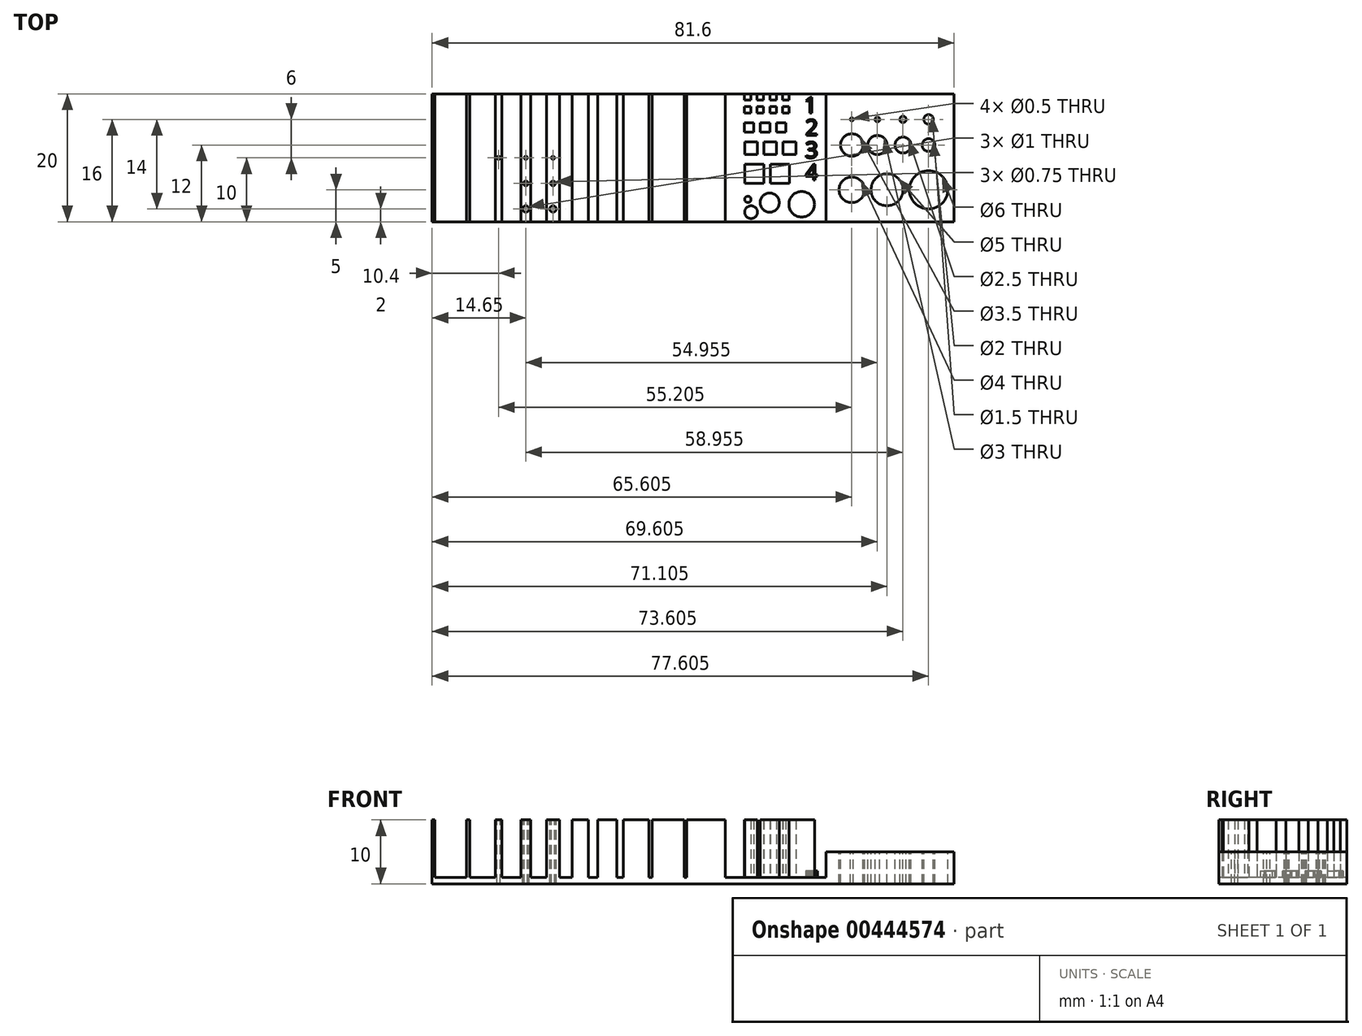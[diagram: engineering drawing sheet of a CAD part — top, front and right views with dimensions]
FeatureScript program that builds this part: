
annotation { "Feature Type Name" : "Feature", "Feature Type Description" : "" }
export const myFeature = defineFeature(function(context is Context, id is Id, definition is map)
    precondition{}
    {
        {
            var Q0;
            Q0=qCreatedBy(makeId("Top.planeOp"),FACE);
            var sketch = newSketch(context, id + "F0", { "sketchPlane" : qUnion([Q0])});
            skLineSegment(sketch, "E0.bottom", {"start": v(0, 0) * mm, "end": v(81.6, 0) * mm});
            skLineSegment(sketch, "E0.top", {"start": v(0, 20) * mm, "end": v(81.6, 20) * mm});
            skLineSegment(sketch, "E0.left", {"start": v(0, 0) * mm, "end": v(0, 20) * mm});
            skLineSegment(sketch, "E0.right", {"start": v(81.6, 0) * mm, "end": v(81.6, 20) * mm});
            skSolve(sketch);
        }
        {
            var Q0;
            Q0=makeQuery(id+"F0.imprint","IMPRINT",FACE,{"disambiguationData":[TD([[makeQuery(id+"F0.imprint","IMPRINT",EDGE,{"derivedFrom":sQuery(id+"F0.wireOp",EDGE,"E0.bottom")}),1.0]])]});
            extrude(context, id + "F1", {"entities" : qUnion([Q0]), "depth" : 1 * mm});
        }
        {
            var Q0;
            Q0=makeQuery(id+"F1.opExtrude","CAP_FACE",FACE,{"disambiguationData":[OSD([sQuery(id+"F0.wireOp",EDGE,"E0.bottom"),sQuery(id+"F0.wireOp",EDGE,"E0.top"),sQuery(id+"F0.wireOp",EDGE,"E0.left"),sQuery(id+"F0.wireOp",EDGE,"E0.right")])],"isStart":false});
            var sketch = newSketch(context, id + "F2", { "sketchPlane" : qUnion([Q0])});
            skLineSegment(sketch, "E1.bottom", {"start": v(0, 20) * mm, "end": v(0.4, 20) * mm});
            skLineSegment(sketch, "E1.top", {"start": v(0, 0) * mm, "end": v(0.4, 0) * mm});
            skLineSegment(sketch, "E1.left", {"start": v(0, 20) * mm, "end": v(0, 0) * mm});
            skLineSegment(sketch, "E1.right", {"start": v(0.4, 20) * mm, "end": v(0.4, 0) * mm});
            skLineSegment(sketch, "E2.bottom", {"start": v(5.4, 20) * mm, "end": v(5.9, 20) * mm});
            skLineSegment(sketch, "E2.top", {"start": v(5.4, 0) * mm, "end": v(5.9, 0) * mm});
            skLineSegment(sketch, "E2.left", {"start": v(5.4, 20) * mm, "end": v(5.4, 0) * mm});
            skLineSegment(sketch, "E2.right", {"start": v(5.9, 20) * mm, "end": v(5.9, 0) * mm});
            skLineSegment(sketch, "E3.bottom", {"start": v(9.9, 20) * mm, "end": v(10.9, 20) * mm});
            skLineSegment(sketch, "E3.top", {"start": v(9.9, 0) * mm, "end": v(10.9, 0) * mm});
            skLineSegment(sketch, "E3.left", {"start": v(9.9, 20) * mm, "end": v(9.9, 0) * mm});
            skLineSegment(sketch, "E3.right", {"start": v(10.9, 20) * mm, "end": v(10.9, 0) * mm});
            skLineSegment(sketch, "E4.bottom", {"start": v(13.9, 20) * mm, "end": v(15.4, 20) * mm});
            skLineSegment(sketch, "E4.top", {"start": v(13.9, 0) * mm, "end": v(15.4, 0) * mm});
            skLineSegment(sketch, "E4.left", {"start": v(13.9, 20) * mm, "end": v(13.9, 0) * mm});
            skLineSegment(sketch, "E4.right", {"start": v(15.4, 20) * mm, "end": v(15.4, 0) * mm});
            skLineSegment(sketch, "E5.bottom", {"start": v(17.9, 20) * mm, "end": v(19.9, 20) * mm});
            skLineSegment(sketch, "E5.top", {"start": v(17.9, 0) * mm, "end": v(19.9, 0) * mm});
            skLineSegment(sketch, "E5.left", {"start": v(17.9, 20) * mm, "end": v(17.9, 0) * mm});
            skLineSegment(sketch, "E5.right", {"start": v(19.9, 20) * mm, "end": v(19.9, 0) * mm});
            skLineSegment(sketch, "E6.bottom", {"start": v(21.9, 20) * mm, "end": v(24.4, 20) * mm});
            skLineSegment(sketch, "E6.top", {"start": v(21.9, 0) * mm, "end": v(24.4, 0) * mm});
            skLineSegment(sketch, "E6.left", {"start": v(21.9, 20) * mm, "end": v(21.9, 0) * mm});
            skLineSegment(sketch, "E6.right", {"start": v(24.4, 20) * mm, "end": v(24.4, 0) * mm});
            skLineSegment(sketch, "E7.bottom", {"start": v(25.9, 20) * mm, "end": v(28.9, 20) * mm});
            skLineSegment(sketch, "E7.top", {"start": v(25.9, 0) * mm, "end": v(28.9, 0) * mm});
            skLineSegment(sketch, "E7.left", {"start": v(25.9, 20) * mm, "end": v(25.9, 0) * mm});
            skLineSegment(sketch, "E7.right", {"start": v(28.9, 20) * mm, "end": v(28.9, 0) * mm});
            skLineSegment(sketch, "E8.bottom", {"start": v(29.9, 20) * mm, "end": v(33.9, 20) * mm});
            skLineSegment(sketch, "E8.top", {"start": v(29.9, 0) * mm, "end": v(33.9, 0) * mm});
            skLineSegment(sketch, "E8.left", {"start": v(29.9, 20) * mm, "end": v(29.9, 0) * mm});
            skLineSegment(sketch, "E8.right", {"start": v(33.9, 20) * mm, "end": v(33.9, 0) * mm});
            skLineSegment(sketch, "E9.bottom", {"start": v(34.4, 20) * mm, "end": v(39.4, 20) * mm});
            skLineSegment(sketch, "E9.top", {"start": v(34.4, 0) * mm, "end": v(39.4, 0) * mm});
            skLineSegment(sketch, "E9.left", {"start": v(34.4, 20) * mm, "end": v(34.4, 0) * mm});
            skLineSegment(sketch, "E9.right", {"start": v(39.4, 20) * mm, "end": v(39.4, 0) * mm});
            skLineSegment(sketch, "E10.bottom", {"start": v(39.8, 20) * mm, "end": v(45.8, 20) * mm});
            skLineSegment(sketch, "E10.top", {"start": v(39.8, 0) * mm, "end": v(45.8, 0) * mm});
            skLineSegment(sketch, "E10.left", {"start": v(39.8, 20) * mm, "end": v(39.8, 0) * mm});
            skLineSegment(sketch, "E10.right", {"start": v(45.8, 20) * mm, "end": v(45.8, 0) * mm});
            skLineSegment(sketch, "E11.bottom", {"start": v(48.8, 20) * mm, "end": v(49.8, 20) * mm});
            skLineSegment(sketch, "E11.top", {"start": v(48.8, 19) * mm, "end": v(49.8, 19) * mm});
            skLineSegment(sketch, "E11.left", {"start": v(48.8, 20) * mm, "end": v(48.8, 19) * mm});
            skLineSegment(sketch, "E11.right", {"start": v(49.8, 20) * mm, "end": v(49.8, 19) * mm});
            skLineSegment(sketch, "E12.bottom", {"start": v(50.8, 20) * mm, "end": v(51.8, 20) * mm});
            skLineSegment(sketch, "E12.top", {"start": v(50.8, 19) * mm, "end": v(51.8, 19) * mm});
            skLineSegment(sketch, "E12.left", {"start": v(50.8, 20) * mm, "end": v(50.8, 19) * mm});
            skLineSegment(sketch, "E12.right", {"start": v(51.8, 20) * mm, "end": v(51.8, 19) * mm});
            skLineSegment(sketch, "E13.bottom", {"start": v(52.8, 20) * mm, "end": v(53.8, 20) * mm});
            skLineSegment(sketch, "E13.top", {"start": v(52.8, 19) * mm, "end": v(53.8, 19) * mm});
            skLineSegment(sketch, "E13.left", {"start": v(52.8, 20) * mm, "end": v(52.8, 19) * mm});
            skLineSegment(sketch, "E13.right", {"start": v(53.8, 20) * mm, "end": v(53.8, 19) * mm});
            skLineSegment(sketch, "E14.bottom", {"start": v(54.8, 20) * mm, "end": v(55.8, 20) * mm});
            skLineSegment(sketch, "E14.top", {"start": v(54.8, 19) * mm, "end": v(55.8, 19) * mm});
            skLineSegment(sketch, "E14.left", {"start": v(54.8, 20) * mm, "end": v(54.8, 19) * mm});
            skLineSegment(sketch, "E14.right", {"start": v(55.8, 20) * mm, "end": v(55.8, 19) * mm});
            skLineSegment(sketch, "E15.bottom", {"start": v(48.8, 18) * mm, "end": v(49.8, 18) * mm});
            skLineSegment(sketch, "E15.top", {"start": v(48.8, 17) * mm, "end": v(49.8, 17) * mm});
            skLineSegment(sketch, "E15.left", {"start": v(48.8, 18) * mm, "end": v(48.8, 17) * mm});
            skLineSegment(sketch, "E15.right", {"start": v(49.8, 18) * mm, "end": v(49.8, 17) * mm});
            skLineSegment(sketch, "E16.bottom", {"start": v(50.8, 18) * mm, "end": v(51.8, 18) * mm});
            skLineSegment(sketch, "E16.top", {"start": v(50.8, 17) * mm, "end": v(51.8, 17) * mm});
            skLineSegment(sketch, "E16.left", {"start": v(50.8, 18) * mm, "end": v(50.8, 17) * mm});
            skLineSegment(sketch, "E16.right", {"start": v(51.8, 18) * mm, "end": v(51.8, 17) * mm});
            skLineSegment(sketch, "E17.bottom", {"start": v(52.8, 18) * mm, "end": v(53.8, 18) * mm});
            skLineSegment(sketch, "E17.top", {"start": v(52.8, 17) * mm, "end": v(53.8, 17) * mm});
            skLineSegment(sketch, "E17.left", {"start": v(52.8, 18) * mm, "end": v(52.8, 17) * mm});
            skLineSegment(sketch, "E17.right", {"start": v(53.8, 18) * mm, "end": v(53.8, 17) * mm});
            skLineSegment(sketch, "E18.bottom", {"start": v(54.8, 18) * mm, "end": v(55.8, 18) * mm});
            skLineSegment(sketch, "E18.top", {"start": v(54.8, 17) * mm, "end": v(55.8, 17) * mm});
            skLineSegment(sketch, "E18.left", {"start": v(54.8, 18) * mm, "end": v(54.8, 17) * mm});
            skLineSegment(sketch, "E18.right", {"start": v(55.8, 18) * mm, "end": v(55.8, 17) * mm});
            skLineSegment(sketch, "E19.bottom", {"start": v(48.8, 15.5) * mm, "end": v(50.3, 15.5) * mm});
            skLineSegment(sketch, "E19.top", {"start": v(48.8, 14) * mm, "end": v(50.3, 14) * mm});
            skLineSegment(sketch, "E19.left", {"start": v(48.8, 15.5) * mm, "end": v(48.8, 14) * mm});
            skLineSegment(sketch, "E19.right", {"start": v(50.3, 15.5) * mm, "end": v(50.3, 14) * mm});
            skLineSegment(sketch, "E20.bottom", {"start": v(51.3, 15.5) * mm, "end": v(52.8, 15.5) * mm});
            skLineSegment(sketch, "E20.top", {"start": v(51.3, 14) * mm, "end": v(52.8, 14) * mm});
            skLineSegment(sketch, "E20.left", {"start": v(51.3, 15.5) * mm, "end": v(51.3, 14) * mm});
            skLineSegment(sketch, "E20.right", {"start": v(52.8, 15.5) * mm, "end": v(52.8, 14) * mm});
            skLineSegment(sketch, "E21.bottom", {"start": v(53.8, 15.5) * mm, "end": v(55.3, 15.5) * mm});
            skLineSegment(sketch, "E21.top", {"start": v(53.8, 14) * mm, "end": v(55.3, 14) * mm});
            skLineSegment(sketch, "E21.left", {"start": v(53.8, 15.5) * mm, "end": v(53.8, 14) * mm});
            skLineSegment(sketch, "E21.right", {"start": v(55.3, 15.5) * mm, "end": v(55.3, 14) * mm});
            skLineSegment(sketch, "E22.bottom", {"start": v(48.86, 12.5) * mm, "end": v(50.86, 12.5) * mm});
            skLineSegment(sketch, "E22.top", {"start": v(48.86, 10.5) * mm, "end": v(50.86, 10.5) * mm});
            skLineSegment(sketch, "E22.left", {"start": v(48.86, 12.5) * mm, "end": v(48.86, 10.5) * mm});
            skLineSegment(sketch, "E22.right", {"start": v(50.86, 12.5) * mm, "end": v(50.86, 10.5) * mm});
            skLineSegment(sketch, "E23.bottom", {"start": v(51.86, 12.5) * mm, "end": v(53.86, 12.5) * mm});
            skLineSegment(sketch, "E23.top", {"start": v(51.86, 10.5) * mm, "end": v(53.86, 10.5) * mm});
            skLineSegment(sketch, "E23.left", {"start": v(51.86, 12.5) * mm, "end": v(51.86, 10.5) * mm});
            skLineSegment(sketch, "E23.right", {"start": v(53.86, 12.5) * mm, "end": v(53.86, 10.5) * mm});
            skLineSegment(sketch, "E24.bottom", {"start": v(54.86, 12.5) * mm, "end": v(56.86, 12.5) * mm});
            skLineSegment(sketch, "E24.top", {"start": v(54.86, 10.5) * mm, "end": v(56.86, 10.5) * mm});
            skLineSegment(sketch, "E24.left", {"start": v(54.86, 12.5) * mm, "end": v(54.86, 10.5) * mm});
            skLineSegment(sketch, "E24.right", {"start": v(56.86, 12.5) * mm, "end": v(56.86, 10.5) * mm});
            skLineSegment(sketch, "E25.bottom", {"start": v(48.86, 9) * mm, "end": v(51.86, 9) * mm});
            skLineSegment(sketch, "E25.top", {"start": v(48.86, 6) * mm, "end": v(51.86, 6) * mm});
            skLineSegment(sketch, "E25.left", {"start": v(48.86, 9) * mm, "end": v(48.86, 6) * mm});
            skLineSegment(sketch, "E25.right", {"start": v(51.86, 9) * mm, "end": v(51.86, 6) * mm});
            skLineSegment(sketch, "E26.bottom", {"start": v(52.86, 9) * mm, "end": v(55.86, 9) * mm});
            skLineSegment(sketch, "E26.top", {"start": v(52.86, 6) * mm, "end": v(55.86, 6) * mm});
            skLineSegment(sketch, "E26.left", {"start": v(52.86, 9) * mm, "end": v(52.86, 6) * mm});
            skLineSegment(sketch, "E26.right", {"start": v(55.86, 9) * mm, "end": v(55.86, 6) * mm});
            skCircle(sketch, "E27", {"center": v(49.36, 3.5) * mm, "radius": 0.5 * mm});
            skCircle(sketch, "E28", {"center": v(49.86, 1.5) * mm, "radius": 1 * mm});
            skCircle(sketch, "E29", {"center": v(52.77, 3) * mm, "radius": 1.5 * mm});
            skCircle(sketch, "E30", {"center": v(57.77, 2.74) * mm, "radius": 2 * mm});
            skSolve(sketch);
        }
        {
            var Q0;
            Q0=makeQuery(id+"F2.imprint","IMPRINT",FACE,{"disambiguationData":[TD([[makeQuery(id+"F2.imprint","IMPRINT",EDGE,{"derivedFrom":sQuery(id+"F2.wireOp",EDGE,"E1.bottom")}),-1.0]])]});
            var Q1;
            Q1=makeQuery(id+"F2.imprint","IMPRINT",FACE,{"disambiguationData":[TD([[makeQuery(id+"F2.imprint","IMPRINT",EDGE,{"derivedFrom":sQuery(id+"F2.wireOp",EDGE,"E2.bottom")}),-1.0]])]});
            var Q2;
            Q2=makeQuery(id+"F2.imprint","IMPRINT",FACE,{"disambiguationData":[TD([[makeQuery(id+"F2.imprint","IMPRINT",EDGE,{"derivedFrom":sQuery(id+"F2.wireOp",EDGE,"E3.bottom")}),-1.0]])]});
            var Q3;
            Q3=makeQuery(id+"F2.imprint","IMPRINT",FACE,{"disambiguationData":[TD([[makeQuery(id+"F2.imprint","IMPRINT",EDGE,{"derivedFrom":sQuery(id+"F2.wireOp",EDGE,"E4.bottom")}),-1.0]])]});
            var Q4;
            Q4=makeQuery(id+"F2.imprint","IMPRINT",FACE,{"disambiguationData":[TD([[makeQuery(id+"F2.imprint","IMPRINT",EDGE,{"derivedFrom":sQuery(id+"F2.wireOp",EDGE,"E5.bottom")}),-1.0]])]});
            var Q5;
            Q5=makeQuery(id+"F2.imprint","IMPRINT",FACE,{"disambiguationData":[TD([[makeQuery(id+"F2.imprint","IMPRINT",EDGE,{"derivedFrom":sQuery(id+"F2.wireOp",EDGE,"E6.bottom")}),-1.0]])]});
            var Q6;
            Q6=makeQuery(id+"F2.imprint","IMPRINT",FACE,{"disambiguationData":[TD([[makeQuery(id+"F2.imprint","IMPRINT",EDGE,{"derivedFrom":sQuery(id+"F2.wireOp",EDGE,"E7.bottom")}),-1.0]])]});
            var Q7;
            Q7=makeQuery(id+"F2.imprint","IMPRINT",FACE,{"disambiguationData":[TD([[makeQuery(id+"F2.imprint","IMPRINT",EDGE,{"derivedFrom":sQuery(id+"F2.wireOp",EDGE,"E8.bottom")}),-1.0]])]});
            var Q8;
            Q8=makeQuery(id+"F2.imprint","IMPRINT",FACE,{"disambiguationData":[TD([[makeQuery(id+"F2.imprint","IMPRINT",EDGE,{"derivedFrom":sQuery(id+"F2.wireOp",EDGE,"E9.bottom")}),-1.0]])]});
            var Q9;
            Q9=makeQuery(id+"F2.imprint","IMPRINT",FACE,{"disambiguationData":[TD([[makeQuery(id+"F2.imprint","IMPRINT",EDGE,{"derivedFrom":sQuery(id+"F2.wireOp",EDGE,"E10.bottom")}),-1.0]])]});
            var Q10;
            Q10=makeQuery(id+"F2.imprint","IMPRINT",FACE,{"disambiguationData":[TD([[makeQuery(id+"F2.imprint","IMPRINT",EDGE,{"derivedFrom":sQuery(id+"F2.wireOp",EDGE,"E15.bottom")}),-1.0]])]});
            var Q11;
            Q11=makeQuery(id+"F2.imprint","IMPRINT",FACE,{"disambiguationData":[TD([[makeQuery(id+"F2.imprint","IMPRINT",EDGE,{"derivedFrom":sQuery(id+"F2.wireOp",EDGE,"E11.bottom")}),-1.0]])]});
            var Q12;
            Q12=makeQuery(id+"F2.imprint","IMPRINT",FACE,{"disambiguationData":[TD([[makeQuery(id+"F2.imprint","IMPRINT",EDGE,{"derivedFrom":sQuery(id+"F2.wireOp",EDGE,"E12.bottom")}),-1.0]])]});
            var Q13;
            Q13=makeQuery(id+"F2.imprint","IMPRINT",FACE,{"disambiguationData":[TD([[makeQuery(id+"F2.imprint","IMPRINT",EDGE,{"derivedFrom":sQuery(id+"F2.wireOp",EDGE,"E13.bottom")}),-1.0]])]});
            var Q14;
            Q14=makeQuery(id+"F2.imprint","IMPRINT",FACE,{"disambiguationData":[TD([[makeQuery(id+"F2.imprint","IMPRINT",EDGE,{"derivedFrom":sQuery(id+"F2.wireOp",EDGE,"E14.bottom")}),-1.0]])]});
            var Q15;
            Q15=makeQuery(id+"F2.imprint","IMPRINT",FACE,{"disambiguationData":[TD([[makeQuery(id+"F2.imprint","IMPRINT",EDGE,{"derivedFrom":sQuery(id+"F2.wireOp",EDGE,"E18.bottom")}),-1.0]])]});
            var Q16;
            Q16=makeQuery(id+"F2.imprint","IMPRINT",FACE,{"disambiguationData":[TD([[makeQuery(id+"F2.imprint","IMPRINT",EDGE,{"derivedFrom":sQuery(id+"F2.wireOp",EDGE,"E17.bottom")}),-1.0]])]});
            var Q17;
            Q17=makeQuery(id+"F2.imprint","IMPRINT",FACE,{"disambiguationData":[TD([[makeQuery(id+"F2.imprint","IMPRINT",EDGE,{"derivedFrom":sQuery(id+"F2.wireOp",EDGE,"E16.bottom")}),-1.0]])]});
            var Q18;
            Q18=makeQuery(id+"F2.imprint","IMPRINT",FACE,{"disambiguationData":[TD([[makeQuery(id+"F2.imprint","IMPRINT",EDGE,{"derivedFrom":sQuery(id+"F2.wireOp",EDGE,"E19.bottom")}),-1.0]])]});
            var Q19;
            Q19=makeQuery(id+"F2.imprint","IMPRINT",FACE,{"disambiguationData":[TD([[makeQuery(id+"F2.imprint","IMPRINT",EDGE,{"derivedFrom":sQuery(id+"F2.wireOp",EDGE,"E20.bottom")}),-1.0]])]});
            var Q20;
            Q20=makeQuery(id+"F2.imprint","IMPRINT",FACE,{"disambiguationData":[TD([[makeQuery(id+"F2.imprint","IMPRINT",EDGE,{"derivedFrom":sQuery(id+"F2.wireOp",EDGE,"E21.bottom")}),-1.0]])]});
            var Q21;
            Q21=makeQuery(id+"F2.imprint","IMPRINT",FACE,{"disambiguationData":[TD([[makeQuery(id+"F2.imprint","IMPRINT",EDGE,{"derivedFrom":sQuery(id+"F2.wireOp",EDGE,"E22.bottom")}),-1.0]])]});
            var Q22;
            Q22=makeQuery(id+"F2.imprint","IMPRINT",FACE,{"disambiguationData":[TD([[makeQuery(id+"F2.imprint","IMPRINT",EDGE,{"derivedFrom":sQuery(id+"F2.wireOp",EDGE,"E23.bottom")}),-1.0]])]});
            var Q23;
            Q23=makeQuery(id+"F2.imprint","IMPRINT",FACE,{"disambiguationData":[TD([[makeQuery(id+"F2.imprint","IMPRINT",EDGE,{"derivedFrom":sQuery(id+"F2.wireOp",EDGE,"E24.bottom")}),-1.0]])]});
            var Q24;
            Q24=makeQuery(id+"F2.imprint","IMPRINT",FACE,{"disambiguationData":[TD([[makeQuery(id+"F2.imprint","IMPRINT",EDGE,{"derivedFrom":sQuery(id+"F2.wireOp",EDGE,"E25.bottom")}),-1.0]])]});
            var Q25;
            Q25=makeQuery(id+"F2.imprint","IMPRINT",FACE,{"disambiguationData":[TD([[makeQuery(id+"F2.imprint","IMPRINT",EDGE,{"derivedFrom":sQuery(id+"F2.wireOp",EDGE,"E26.bottom")}),-1.0]])]});
            var Q26;
            Q26=makeQuery(id+"F2.imprint","IMPRINT",FACE,{"disambiguationData":[TD([[makeQuery(id+"F2.imprint","IMPRINT",EDGE,{"derivedFrom":sQuery(id+"F2.wireOp",EDGE,"E27")}),1.0]])]});
            var Q27;
            Q27=makeQuery(id+"F2.imprint","IMPRINT",FACE,{"disambiguationData":[TD([[makeQuery(id+"F2.imprint","IMPRINT",EDGE,{"derivedFrom":sQuery(id+"F2.wireOp",EDGE,"E28")}),1.0]])]});
            var Q28;
            Q28=makeQuery(id+"F2.imprint","IMPRINT",FACE,{"disambiguationData":[TD([[makeQuery(id+"F2.imprint","IMPRINT",EDGE,{"derivedFrom":sQuery(id+"F2.wireOp",EDGE,"E29")}),1.0]])]});
            var Q29;
            Q29=makeQuery(id+"F2.imprint","IMPRINT",FACE,{"disambiguationData":[TD([[makeQuery(id+"F2.imprint","IMPRINT",EDGE,{"derivedFrom":sQuery(id+"F2.wireOp",EDGE,"E30")}),1.0]])]});
            extrude(context, id + "F3", {"entities" : qUnion([Q0, Q1, Q2, Q3, Q4, Q5, Q6, Q7, Q8, Q9, Q10, Q11, Q12, Q13, Q14, Q15, Q16, Q17, Q18, Q19, Q20, Q21, Q22, Q23, Q24, Q25, Q26, Q27, Q28, Q29]), "operationType" : NewBodyOperationType.ADD, "depth" : 9 * mm});
        }
        {
            var Q0;
            {var subQ0=sQuery(id+"F0.wireOp",EDGE,"E0.right");var subQ1=sQuery(id+"F0.wireOp",EDGE,"E0.top");var subQ2=sQuery(id+"F0.wireOp",EDGE,"E0.bottom");Q0=makeQuery(id+"F3.boolean.opBoolean","SPLIT",FACE,{"disambiguationData":[TD([makeQuery(id+"F1.opExtrude","SWEPT_FACE",FACE,{"disambiguationData":[OSD([subQ0])]})])],"derivedFrom":makeQuery(id+"F1.opExtrude","CAP_FACE",FACE,{"disambiguationData":[OSD([subQ2,subQ1,sQuery(id+"F0.wireOp",EDGE,"E0.left"),subQ0])],"isStart":false})});}
            var sketch = newSketch(context, id + "F4", { "sketchPlane" : qUnion([Q0])});
            skLineSegment(sketch, "E31.bottom", {"start": v(81.6, 20) * mm, "end": v(61.6, 20) * mm});
            skLineSegment(sketch, "E31.top", {"start": v(81.6, 0) * mm, "end": v(61.6, 0) * mm});
            skLineSegment(sketch, "E31.left", {"start": v(81.6, 20) * mm, "end": v(81.6, 0) * mm});
            skLineSegment(sketch, "E31.right", {"start": v(61.6, 20) * mm, "end": v(61.6, 0) * mm});
            skSolve(sketch);
        }
        {
            var Q0;
            Q0=makeQuery(id+"F4.imprint","IMPRINT",FACE,{"disambiguationData":[TD([[makeQuery(id+"F4.imprint","IMPRINT",EDGE,{"derivedFrom":sQuery(id+"F4.wireOp",EDGE,"E31.bottom")}),-1.0]])]});
            extrude(context, id + "F5", {"entities" : qUnion([Q0]), "operationType" : NewBodyOperationType.ADD, "depth" : 4 * mm});
        }
        {
            var Q0;
            Q0=makeQuery(id+"F3.opExtrude","CAP_FACE",FACE,{"disambiguationData":[OSD([sQuery(id+"F2.wireOp",EDGE,"E3.bottom"),sQuery(id+"F2.wireOp",EDGE,"E3.top"),sQuery(id+"F2.wireOp",EDGE,"E3.left"),sQuery(id+"F2.wireOp",EDGE,"E3.right")])],"isStart":false});
            var sketch = newSketch(context, id + "F6", { "sketchPlane" : qUnion([Q0])});
            skCircle(sketch, "E32", {"center": v(10.4, 10) * mm, "radius": 0.25 * mm});
            skSolve(sketch);
        }
        {
            var Q0;
            Q0=makeQuery(id+"F6.imprint","IMPRINT",FACE,{"disambiguationData":[TD([[makeQuery(id+"F6.imprint","IMPRINT",EDGE,{"derivedFrom":sQuery(id+"F6.wireOp",EDGE,"E32")}),1.0]])]});
            extrude(context, id + "F7", {"entities" : qUnion([Q0]), "operationType" : NewBodyOperationType.REMOVE, "endBound" : BoundingType.THROUGH_ALL, "oppositeDirection" : true, "depth" : 25 * mm});
        }
        {
            var Q0;
            Q0=makeQuery(id+"F3.opExtrude","CAP_FACE",FACE,{"disambiguationData":[OSD([sQuery(id+"F2.wireOp",EDGE,"E4.bottom"),sQuery(id+"F2.wireOp",EDGE,"E4.top"),sQuery(id+"F2.wireOp",EDGE,"E4.left"),sQuery(id+"F2.wireOp",EDGE,"E4.right")])],"isStart":false});
            var sketch = newSketch(context, id + "F8", { "sketchPlane" : qUnion([Q0])});
            skCircle(sketch, "E33", {"center": v(14.65, 10) * mm, "radius": 0.25 * mm});
            skCircle(sketch, "E34", {"center": v(14.65, 6) * mm, "radius": 0.38 * mm});
            skCircle(sketch, "E35", {"center": v(14.65, 2) * mm, "radius": 0.5 * mm});
            skSolve(sketch);
        }
        {
            var Q0;
            Q0=makeQuery(id+"F8.imprint","IMPRINT",FACE,{"disambiguationData":[TD([[makeQuery(id+"F8.imprint","IMPRINT",EDGE,{"derivedFrom":sQuery(id+"F8.wireOp",EDGE,"E33")}),1.0]])]});
            var Q1;
            Q1=makeQuery(id+"F8.imprint","IMPRINT",FACE,{"disambiguationData":[TD([[makeQuery(id+"F8.imprint","IMPRINT",EDGE,{"derivedFrom":sQuery(id+"F8.wireOp",EDGE,"E34")}),1.0]])]});
            var Q2;
            Q2=makeQuery(id+"F8.imprint","IMPRINT",FACE,{"disambiguationData":[TD([[makeQuery(id+"F8.imprint","IMPRINT",EDGE,{"derivedFrom":sQuery(id+"F8.wireOp",EDGE,"E35")}),1.0]])]});
            extrude(context, id + "F9", {"entities" : qUnion([Q0, Q1, Q2]), "operationType" : NewBodyOperationType.REMOVE, "endBound" : BoundingType.THROUGH_ALL, "oppositeDirection" : true, "depth" : 25 * mm});
        }
        {
            var Q0;
            Q0=makeQuery(id+"F3.opExtrude","CAP_FACE",FACE,{"disambiguationData":[OSD([sQuery(id+"F2.wireOp",EDGE,"E5.bottom"),sQuery(id+"F2.wireOp",EDGE,"E5.top"),sQuery(id+"F2.wireOp",EDGE,"E5.left"),sQuery(id+"F2.wireOp",EDGE,"E5.right")])],"isStart":false});
            var sketch = newSketch(context, id + "F10", { "sketchPlane" : qUnion([Q0])});
            skCircle(sketch, "E36", {"center": v(18.9, 10) * mm, "radius": 0.25 * mm});
            skCircle(sketch, "E37", {"center": v(18.9, 6) * mm, "radius": 0.38 * mm});
            skCircle(sketch, "E38", {"center": v(18.9, 2) * mm, "radius": 0.5 * mm});
            skSolve(sketch);
        }
        {
            var Q0;
            Q0=makeQuery(id+"F10.imprint","IMPRINT",FACE,{"disambiguationData":[TD([[makeQuery(id+"F10.imprint","IMPRINT",EDGE,{"derivedFrom":sQuery(id+"F10.wireOp",EDGE,"E36")}),1.0]])]});
            var Q1;
            Q1=makeQuery(id+"F10.imprint","IMPRINT",FACE,{"disambiguationData":[TD([[makeQuery(id+"F10.imprint","IMPRINT",EDGE,{"derivedFrom":sQuery(id+"F10.wireOp",EDGE,"E37")}),1.0]])]});
            var Q2;
            Q2=makeQuery(id+"F10.imprint","IMPRINT",FACE,{"disambiguationData":[TD([[makeQuery(id+"F10.imprint","IMPRINT",EDGE,{"derivedFrom":sQuery(id+"F10.wireOp",EDGE,"E38")}),1.0]])]});
            extrude(context, id + "F11", {"entities" : qUnion([Q0, Q1, Q2]), "operationType" : NewBodyOperationType.REMOVE, "endBound" : BoundingType.THROUGH_ALL, "oppositeDirection" : true, "depth" : 25 * mm});
        }
        {
            var Q0;
            Q0=makeQuery(id+"F5.opExtrude","CAP_FACE",FACE,{"disambiguationData":[OSD([sQuery(id+"F4.wireOp",EDGE,"E31.bottom"),sQuery(id+"F4.wireOp",EDGE,"E31.top"),sQuery(id+"F4.wireOp",EDGE,"E31.left"),sQuery(id+"F4.wireOp",EDGE,"E31.right")])],"isStart":false});
            var sketch = newSketch(context, id + "F12", { "sketchPlane" : qUnion([Q0])});
            skCircle(sketch, "E39", {"center": v(65.6, 16) * mm, "radius": 0.25 * mm});
            skCircle(sketch, "E40", {"center": v(69.6, 16) * mm, "radius": 0.38 * mm});
            skCircle(sketch, "E41", {"center": v(73.6, 16) * mm, "radius": 0.5 * mm});
            skCircle(sketch, "E42", {"center": v(77.6, 16) * mm, "radius": 0.75 * mm});
            skCircle(sketch, "E43", {"center": v(77.6, 12) * mm, "radius": 1 * mm});
            skCircle(sketch, "E44", {"center": v(73.6, 12) * mm, "radius": 1.25 * mm});
            skCircle(sketch, "E45", {"center": v(69.6, 12) * mm, "radius": 1.5 * mm});
            skCircle(sketch, "E46", {"center": v(65.6, 12) * mm, "radius": 1.75 * mm});
            skCircle(sketch, "E47", {"center": v(65.6, 5) * mm, "radius": 2 * mm});
            skCircle(sketch, "E48", {"center": v(71.1, 5) * mm, "radius": 2.5 * mm});
            skCircle(sketch, "E49", {"center": v(77.6, 5) * mm, "radius": 3 * mm});
            skSolve(sketch);
        }
        {
            var Q0;
            Q0=makeQuery(id+"F12.imprint","IMPRINT",FACE,{"disambiguationData":[TD([[makeQuery(id+"F12.imprint","IMPRINT",EDGE,{"derivedFrom":sQuery(id+"F12.wireOp",EDGE,"E49")}),1.0]])]});
            var Q1;
            Q1=makeQuery(id+"F12.imprint","IMPRINT",FACE,{"disambiguationData":[TD([[makeQuery(id+"F12.imprint","IMPRINT",EDGE,{"derivedFrom":sQuery(id+"F12.wireOp",EDGE,"E41")}),1.0]])]});
            var Q2;
            Q2=makeQuery(id+"F12.imprint","IMPRINT",FACE,{"disambiguationData":[TD([[makeQuery(id+"F12.imprint","IMPRINT",EDGE,{"derivedFrom":sQuery(id+"F12.wireOp",EDGE,"E47")}),1.0]])]});
            var Q3;
            Q3=makeQuery(id+"F12.imprint","IMPRINT",FACE,{"disambiguationData":[TD([[makeQuery(id+"F12.imprint","IMPRINT",EDGE,{"derivedFrom":sQuery(id+"F12.wireOp",EDGE,"E43")}),1.0]])]});
            var Q4;
            Q4=makeQuery(id+"F12.imprint","IMPRINT",FACE,{"disambiguationData":[TD([[makeQuery(id+"F12.imprint","IMPRINT",EDGE,{"derivedFrom":sQuery(id+"F12.wireOp",EDGE,"E46")}),1.0]])]});
            var Q5;
            Q5=makeQuery(id+"F12.imprint","IMPRINT",FACE,{"disambiguationData":[TD([[makeQuery(id+"F12.imprint","IMPRINT",EDGE,{"derivedFrom":sQuery(id+"F12.wireOp",EDGE,"E39")}),1.0]])]});
            var Q6;
            Q6=makeQuery(id+"F12.imprint","IMPRINT",FACE,{"disambiguationData":[TD([[makeQuery(id+"F12.imprint","IMPRINT",EDGE,{"derivedFrom":sQuery(id+"F12.wireOp",EDGE,"E40")}),1.0]])]});
            var Q7;
            Q7=makeQuery(id+"F12.imprint","IMPRINT",FACE,{"disambiguationData":[TD([[makeQuery(id+"F12.imprint","IMPRINT",EDGE,{"derivedFrom":sQuery(id+"F12.wireOp",EDGE,"E45")}),1.0]])]});
            var Q8;
            Q8=makeQuery(id+"F12.imprint","IMPRINT",FACE,{"disambiguationData":[TD([[makeQuery(id+"F12.imprint","IMPRINT",EDGE,{"derivedFrom":sQuery(id+"F12.wireOp",EDGE,"E42")}),1.0]])]});
            var Q9;
            Q9=makeQuery(id+"F12.imprint","IMPRINT",FACE,{"disambiguationData":[TD([[makeQuery(id+"F12.imprint","IMPRINT",EDGE,{"derivedFrom":sQuery(id+"F12.wireOp",EDGE,"E44")}),1.0]])]});
            var Q10;
            Q10=makeQuery(id+"F12.imprint","IMPRINT",FACE,{"disambiguationData":[TD([[makeQuery(id+"F12.imprint","IMPRINT",EDGE,{"derivedFrom":sQuery(id+"F12.wireOp",EDGE,"E48")}),1.0]])]});
            extrude(context, id + "F13", {"entities" : qUnion([Q0, Q1, Q2, Q3, Q4, Q5, Q6, Q7, Q8, Q9, Q10]), "operationType" : NewBodyOperationType.REMOVE, "endBound" : BoundingType.THROUGH_ALL, "oppositeDirection" : true, "depth" : 25 * mm});
        }
        {
            var Q0;
            {var subQ0=sQuery(id+"F0.wireOp",EDGE,"E0.right");var subQ1=sQuery(id+"F0.wireOp",EDGE,"E0.top");var subQ2=sQuery(id+"F0.wireOp",EDGE,"E0.bottom");Q0=makeQuery(id+"F3.boolean.opBoolean","SPLIT",FACE,{"disambiguationData":[TD([makeQuery(id+"F1.opExtrude","SWEPT_FACE",FACE,{"disambiguationData":[OSD([subQ0])]})])],"derivedFrom":makeQuery(id+"F1.opExtrude","CAP_FACE",FACE,{"disambiguationData":[OSD([subQ2,subQ1,sQuery(id+"F0.wireOp",EDGE,"E0.left"),subQ0])],"isStart":false})});}
            var sketch = newSketch(context, id + "F14", { "sketchPlane" : qUnion([Q0])});
            skText(sketch, "E50", { "text": "1", "fontName": "OpenSans-Regular.ttf"});
            skText(sketch, "E51", { "text": "2", "fontName": "OpenSans-Regular.ttf"});
            skText(sketch, "E52", { "text": "3", "fontName": "OpenSans-Regular.ttf"});
            skText(sketch, "E53", { "text": "4", "fontName": "OpenSans-Regular.ttf"});
            const initialGuessF14  = {"E50": [0.05812, 0.017, 1, 0, 0.0025], "E51": [0.05833, 0.0135, 1, 0, 0.0025], "E52": [0.05833, 0.01, 1, 0, 0.0025], "E53": [0.05833, 0.0065, 1, 0, 0.0025]};
            skSetInitialGuess(sketch, initialGuessF14);
            skSolve(sketch);
        }
        {
            var Q0;
            Q0=makeQuery(id+"F14.imprint","IMPRINT",FACE,{"disambiguationData":[TD([[makeQuery(id+"F14.imprint","IMPRINT",EDGE,{"derivedFrom":sQuery(id+"F14.wireOp",EDGE,"E53.sketch_text.stroke-0")}),-1.0]])]});
            var Q1;
            Q1=makeQuery(id+"F14.imprint","IMPRINT",FACE,{"disambiguationData":[TD([[makeQuery(id+"F14.imprint","IMPRINT",EDGE,{"derivedFrom":sQuery(id+"F14.wireOp",EDGE,"E52.sketch_text.stroke-0")}),-1.0]])]});
            var Q2;
            Q2=makeQuery(id+"F14.imprint","IMPRINT",FACE,{"disambiguationData":[TD([[makeQuery(id+"F14.imprint","IMPRINT",EDGE,{"derivedFrom":sQuery(id+"F14.wireOp",EDGE,"E50.sketch_text.stroke-0")}),-1.0]])]});
            var Q3;
            Q3=makeQuery(id+"F14.imprint","IMPRINT",FACE,{"disambiguationData":[TD([[makeQuery(id+"F14.imprint","IMPRINT",EDGE,{"derivedFrom":sQuery(id+"F14.wireOp",EDGE,"E51.sketch_text.stroke-0")}),-1.0]])]});
            extrude(context, id + "F15", {"entities" : qUnion([Q0, Q1, Q2, Q3]), "operationType" : NewBodyOperationType.ADD, "depth" : 1 * mm});
        }
    });
